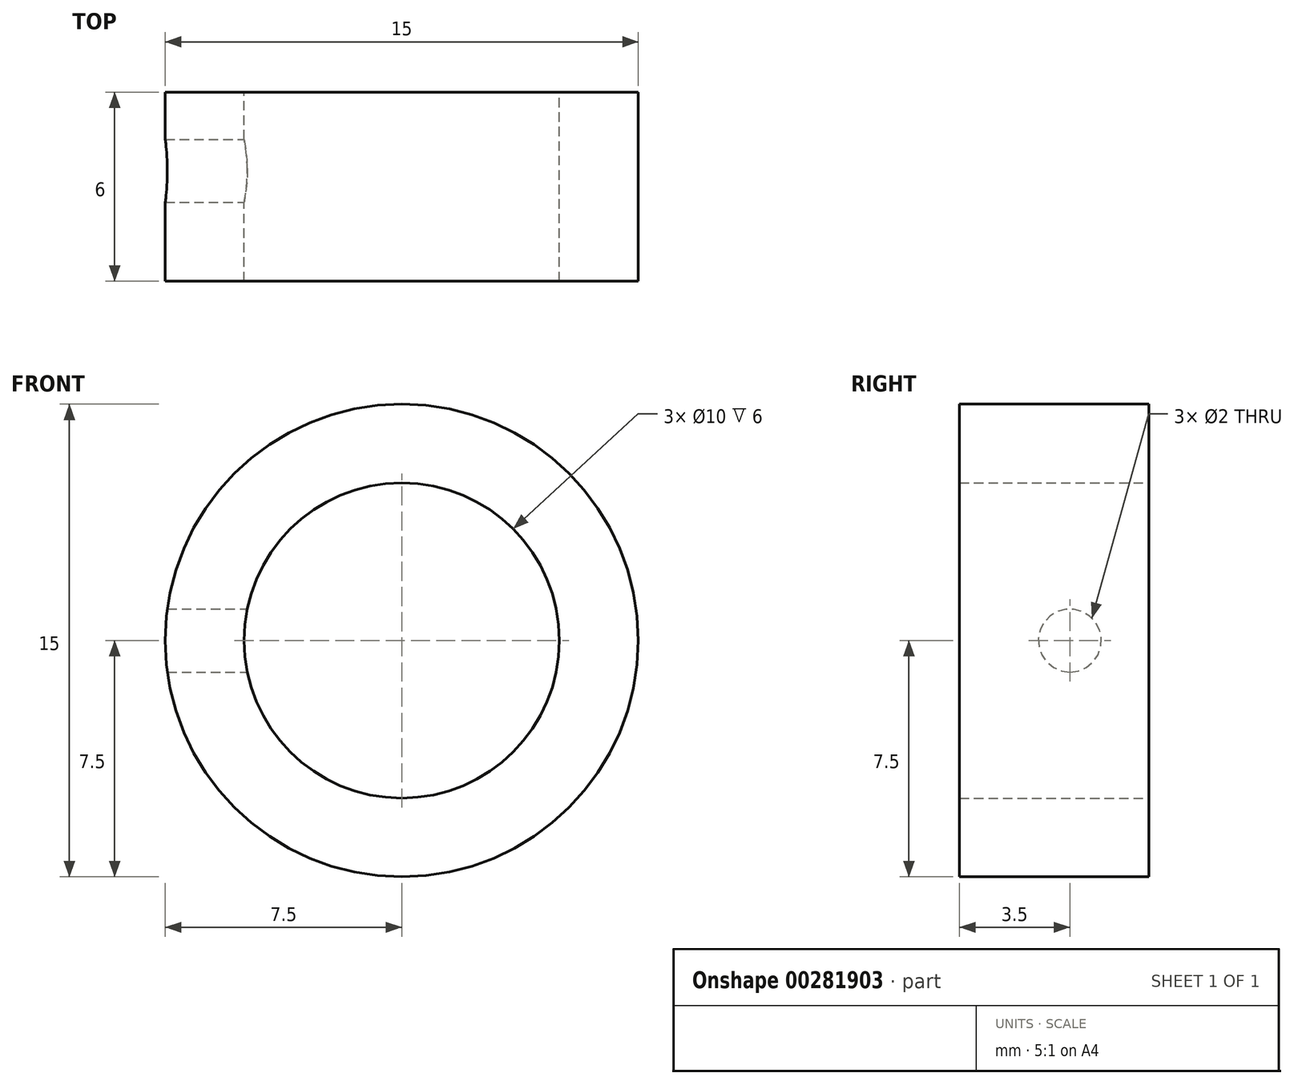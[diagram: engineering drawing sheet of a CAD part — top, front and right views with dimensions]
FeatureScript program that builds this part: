
annotation { "Feature Type Name" : "Feature", "Feature Type Description" : "" }
export const myFeature = defineFeature(function(context is Context, id is Id, definition is map)
    precondition{}
    {
        {
            var Q0;
            Q0=qCreatedBy(makeId("Front.planeOp"),FACE);
            var sketch = newSketch(context, id + "F0", { "sketchPlane" : qUnion([Q0])});
            skCircle(sketch, "E0", {"center": v(0, 0) * mm, "radius": 7.5 * mm});
            skCircle(sketch, "E1", {"center": v(0, 0) * mm, "radius": 5 * mm});
            skSolve(sketch);
        }
        {
            var Q0;
            Q0=qSketchRegion(id+"F0",true);
            extrude(context, id + "F1", {"entities" : qUnion([Q0]), "depth" : 6 * mm});
        }
        {
            var Q0;
            Q0=qCreatedBy(makeId("Right.planeOp"),FACE);
            var sketch = newSketch(context, id + "F2", { "sketchPlane" : qUnion([Q0])});
            skCircle(sketch, "E2", {"center": v(-2.5, 0) * mm, "radius": 1 * mm});
            skSolve(sketch);
        }
        {
            var Q0;
            Q0=qSketchRegion(id+"F2",true);
            extrude(context, id + "F3", {"entities" : qUnion([Q0]), "operationType" : NewBodyOperationType.REMOVE, "oppositeDirection" : true, "depth" : 25 * mm});
        }
    });
